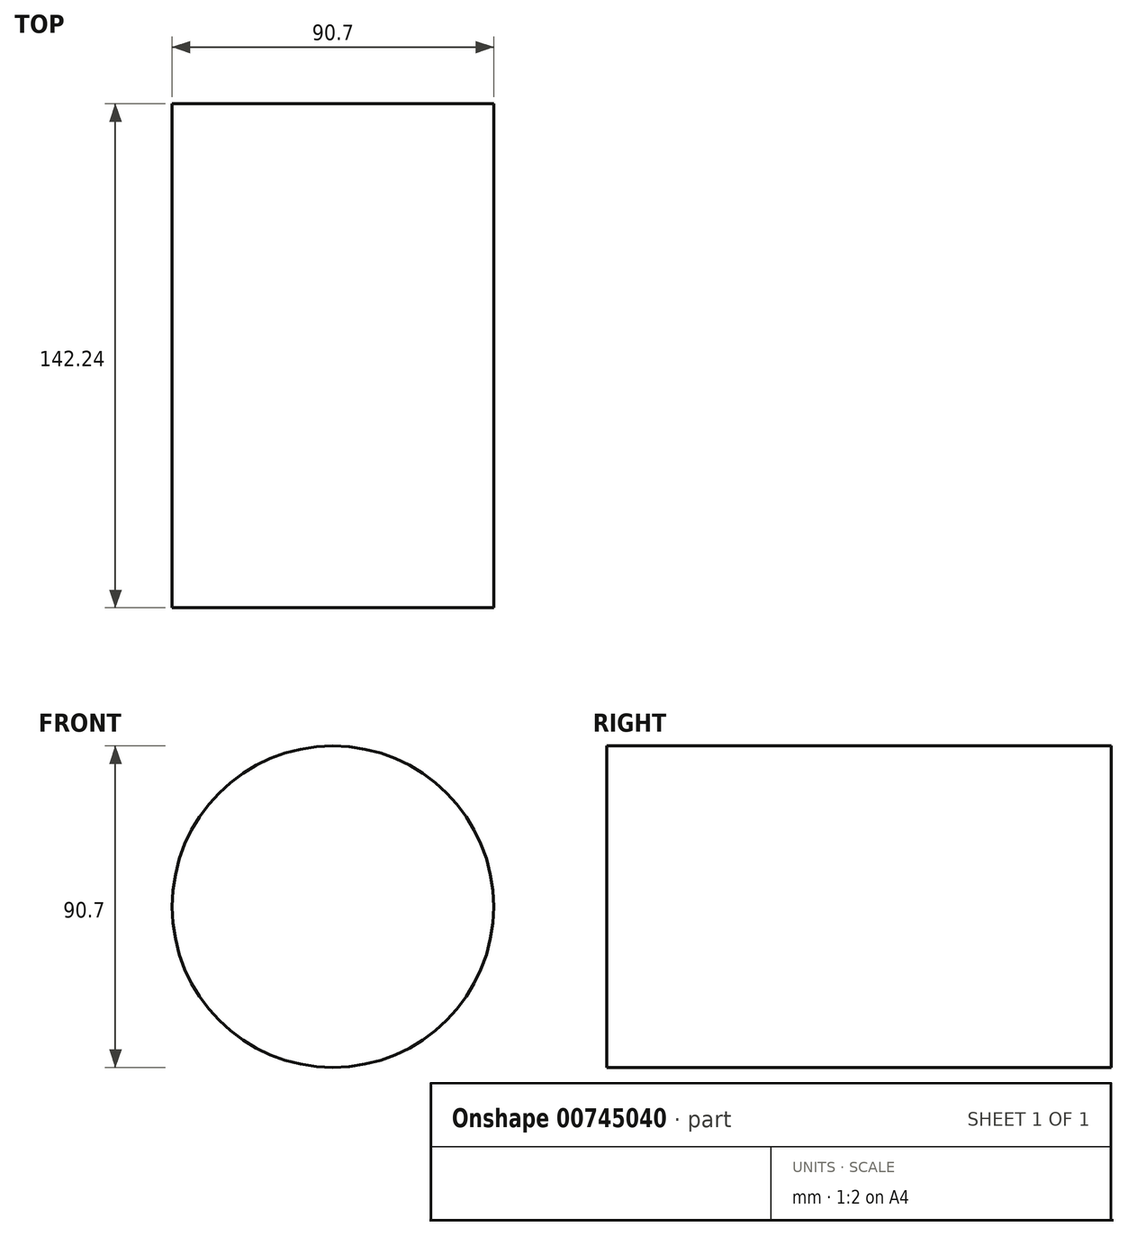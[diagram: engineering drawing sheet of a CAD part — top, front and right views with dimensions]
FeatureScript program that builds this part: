
annotation { "Feature Type Name" : "Feature", "Feature Type Description" : "" }
export const myFeature = defineFeature(function(context is Context, id is Id, definition is map)
    precondition{}
    {
        {
            var Q0;
            Q0=qCreatedBy(makeId("Front.planeOp"),FACE);
            var sketch = newSketch(context, id + "F0", { "sketchPlane" : qUnion([Q0])});
            skCircle(sketch, "E0", {"center": v(-11, 0) * mm, "radius": 45.35 * mm});
            skCircle(sketch, "E1", {"center": v(-11, 0) * mm, "radius": 11 * mm});
            skSolve(sketch);
        }
        {
            var Q0;
            Q0=makeQuery(id+"F0.imprint","IMPRINT",FACE,{"disambiguationData":[TD([[makeQuery(id+"F0.imprint","IMPRINT",EDGE,{"derivedFrom":sQuery(id+"F0.wireOp",EDGE,"E0")}),1.0]])]});
            var Q1;
            Q1=makeQuery(id+"F0.imprint","IMPRINT",FACE,{"disambiguationData":[TD([[makeQuery(id+"F0.imprint","IMPRINT",EDGE,{"derivedFrom":sQuery(id+"F0.wireOp",EDGE,"E1")}),1.0]])]});
            extrude(context, id + "F1", {"entities" : qUnion([Q0, Q1]), "endBound" : BoundingType.SYMMETRIC, "depth" : 142.24 * mm, "offsetDistance" : 25.4 * mm});
        }
        {
            var Q0;
            Q0=sQuery(id+"F0.wireOp",EDGE,"E1");
            extrude(context, id + "F2", {"bodyType" : ToolBodyType.SURFACE, "surfaceEntities" : qUnion([Q0]), "endBound" : BoundingType.SYMMETRIC, "oppositeDirection" : true, "depth" : 219.46 * mm, "offsetDistance" : 25.4 * mm});
        }
    });
